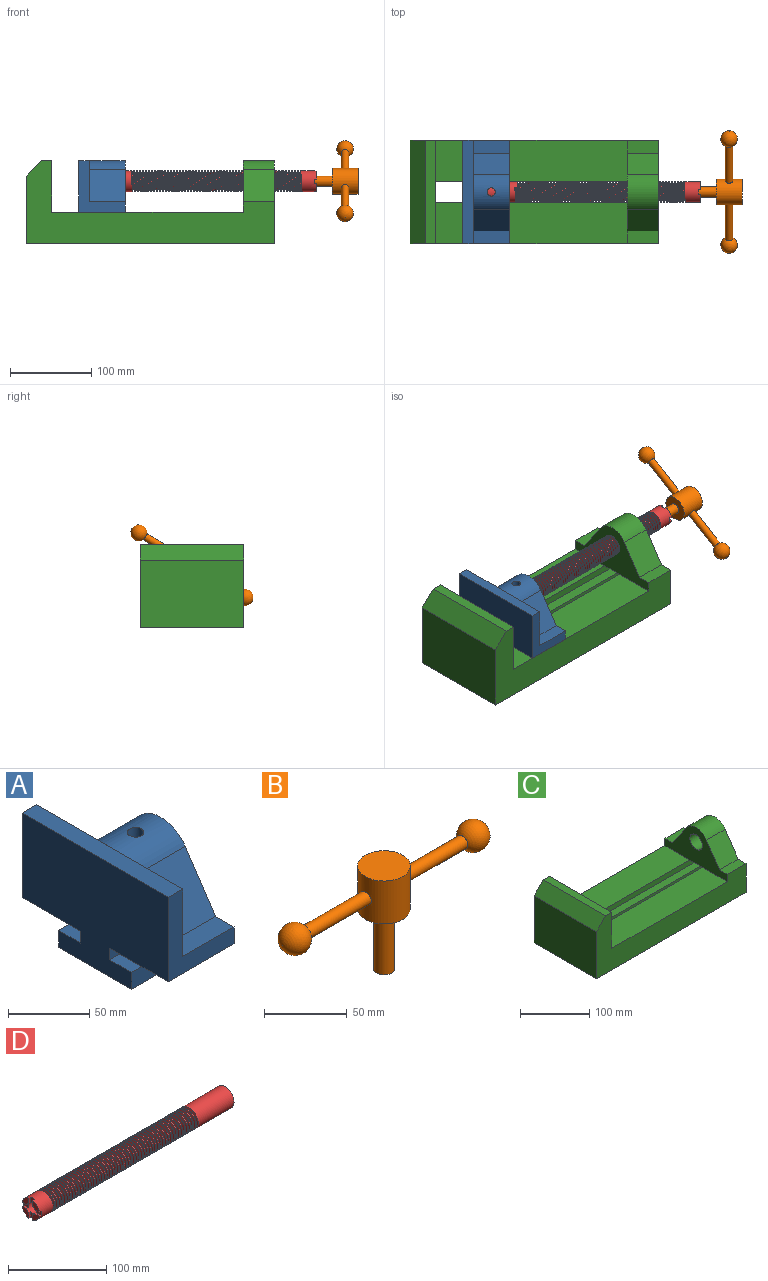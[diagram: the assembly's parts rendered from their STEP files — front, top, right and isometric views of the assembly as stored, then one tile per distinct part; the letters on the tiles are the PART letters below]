
ASSEMBLY  parts=4 mates=3
PART A: 24 faces, bbox 57.2x127x85.1 mm
  f0: cylinder r=25.4mm len=44.45mm, axis (1,0,0), area 2131.1mm2, adj f1,f7,f9,f11,f12,f23
  f1: plane 127x85.09mm, normal (1,0,0), area 5190mm2, adj f0,f2,f3,f5,f7,f8,f10,f11
  f2: plane 63.5x57.15mm, normal (0,0,-1), area 3629mm2, adj f1,f6,f18,f19
  f3: plane 63.5x57.15mm, normal (0,-1,0), area 1371mm2, adj f1,f4,f6,f10,f12,f22
  f4: plane 127x12.7mm, normal (0,0,1), area 1612.9mm2, adj f3,f5,f6,f9,f12
  f5: plane 63.5x57.15mm, normal (0,1,0), area 1371mm2, adj f1,f4,f6,f8,f9,f15
  f6: plane 127x85.09mm, normal (-1,0,0), area 9096.8mm2, adj f2,f3,f4,f5,f15,f16,f17,f18
  f7: plane 44.45x39.55mm, normal (0,0.83,0.56), area 2116.9mm2, adj f0,f1,f8,f9
  f8: plane 44.45x15.88mm, normal (0,0,1), area 705.6mm2, adj f1,f5,f7,f9
  f9: plane 63.5x50.8mm, normal (1,0,0), area 1700mm2, adj f0,f4,f5,f7,f8
  f10: plane 44.45x15.88mm, normal (0,0,1), area 705.6mm2, adj f1,f3,f11,f12
  f11: plane 44.45x39.55mm, normal (0,-0.83,0.56), area 2116.9mm2, adj f0,f1,f10,f12
  f12: plane 63.5x50.8mm, normal (1,0,0), area 1700mm2, adj f0,f3,f4,f10,f11
  f13: cylinder r=12.7mm len=44.45mm, axis (1,0,0), area 3464.1mm2, adj f1,f14,f23
  f14: plane 25.4x25.4mm, normal (1,0,0), area 506.7mm2, adj f13
  f15: plane 57.15x50.8mm, normal (0,0,-1), area 2903.2mm2, adj f1,f5,f6,f16
  f16: plane 57.15x8.89mm, normal (0,1,0), area 508.1mm2, adj f1,f6,f15,f17
  f17: plane 57.15x19.05mm, normal (0,0,1), area 1088.7mm2, adj f1,f6,f16,f18
  f18: plane 57.15x12.7mm, normal (0,1,0), area 725.8mm2, adj f1,f2,f6,f17
  f19: plane 57.15x12.7mm, normal (0,-1,0), area 725.8mm2, adj f1,f2,f6,f20
  f20: plane 57.15x19.05mm, normal (0,0,1), area 1088.7mm2, adj f1,f6,f19,f21
  f21: plane 57.15x8.89mm, normal (0,-1,0), area 508.1mm2, adj f1,f6,f20,f22
  f22: plane 57.15x50.8mm, normal (0,0,-1), area 2903.2mm2, adj f1,f3,f6,f21
  f23: cylinder r=5.08mm len=13.76mm, axis (0,0,1), area 413.9mm2, adj f0,f13
PART B: 9 faces, bbox 172.7x31.8x76.2 mm
  f0: cylinder r=4.45mm len=51.82mm, axis (-1,0,0), area 1438.5mm2, adj f2,f8
  f1: cylinder r=4.45mm len=51.82mm, axis (-1,0,0), area 1438.5mm2, adj f2,f7
  f2: cylinder r=15.88mm len=31.75mm, axis (0,0,1), area 3041.6mm2, adj f0,f1,f3,f4
  f3: plane 31.75x31.75mm, normal (0,0,-1), area 665.1mm2, adj f2,f5
  f4: plane 31.75x31.75mm, normal (0,0,1), area 791.7mm2, adj f2
  f5: cylinder r=6.35mm len=44.45mm, axis (0,0,1), area 1773.5mm2, adj f3,f6
  f6: plane 12.7x12.7mm, normal (0,0,-1), area 126.7mm2, adj f5
  f7: sphere r=10.16mm, area 1231.8mm2, adj f1
  f8: sphere r=10.16mm, area 1231.8mm2, adj f0
PART C: 28 faces, bbox 304.8x127x101.6 mm
  f0: plane 127x101.6mm, normal (1,0,0), area 7544.8mm2, adj f7,f8,f9,f10,f11,f12,f13,f14
  f1: plane 234.95x50.8mm, normal (0,0,1), area 11935.5mm2, adj f2,f4,f9,f21
  f2: plane 127x63.5mm, normal (-1,0,0), area 4157.7mm2, adj f1,f3,f8,f9,f10,f11,f12,f13
  f3: plane 234.95x50.8mm, normal (0,0,1), area 11935.5mm2, adj f2,f4,f8,f22
  f4: plane 127x101.6mm, normal (1,0,0), area 9516.1mm2, adj f1,f3,f5,f7,f8,f9,f17,f18
  f5: plane 127x12.7mm, normal (0,0,1), area 1612.9mm2, adj f4,f8,f9,f27
  f6: plane 127x82.55mm, normal (-1,0,0), area 10483.8mm2, adj f7,f8,f9,f27
  f7: plane 304.8x127mm, normal (0,0,-1), area 31774.1mm2, adj f0,f4,f6,f8,f9,f17,f26
  f8: plane 304.8x101.6mm, normal (0,-1,0), area 13931.4mm2, adj f0,f2,f3,f4,f5,f6,f7,f13
  f9: plane 304.8x101.6mm, normal (0,1,0), area 13931.4mm2, adj f0,f1,f2,f4,f5,f6,f7,f11
  f10: cylinder r=25.4mm len=42.19mm, axis (1,0,0), area 1896.6mm2, adj f0,f2,f12,f14
  f11: plane 38.1x15.88mm, normal (0,0,1), area 604.8mm2, adj f0,f2,f9,f12
  f12: plane 39.55x38.1mm, normal (0,0.83,0.56), area 1814.5mm2, adj f0,f2,f10,f11
  f13: plane 38.1x15.88mm, normal (0,0,1), area 604.8mm2, adj f0,f2,f8,f14
  f14: plane 39.55x38.1mm, normal (0,-0.83,0.56), area 1814.5mm2, adj f0,f2,f10,f13
  f15: cylinder r=12.7mm len=38.1mm, axis (1,0,0), area 3040.2mm2, adj f0,f2
  f16: plane 38.1x25.4mm, normal (0,0,-1), area 967.7mm2, adj f0,f2,f21,f22
  f17: plane 273.05x16.51mm, normal (0,-1,0), area 4508.1mm2, adj f0,f4,f7,f18
  f18: plane 273.05x19.05mm, normal (0,0,1), area 5201.6mm2, adj f0,f4,f17,f19
  f19: plane 273.05x12.7mm, normal (0,-1,0), area 3467.7mm2, adj f0,f4,f18,f20
  f20: plane 273.05x19.05mm, normal (0,0,-1), area 5201.6mm2, adj f0,f4,f19,f21
  f21: plane 273.05x8.89mm, normal (0,-1,0), area 2427.4mm2, adj f0,f1,f4,f16,f20
  f22: plane 273.05x8.89mm, normal (0,1,0), area 2427.4mm2, adj f0,f3,f4,f16,f23
  f23: plane 273.05x19.05mm, normal (0,0,-1), area 5201.6mm2, adj f0,f4,f22,f24
  f24: plane 273.05x12.7mm, normal (0,1,0), area 3467.7mm2, adj f0,f4,f23,f25
  f25: plane 273.05x19.05mm, normal (0,0,1), area 5201.6mm2, adj f0,f4,f24,f26
  f26: plane 273.05x16.51mm, normal (0,1,0), area 4508.1mm2, adj f0,f4,f7,f25
  f27: plane 127x19.05mm, normal (-0.71,0,0.71), area 3421.5mm2, adj f5,f6,f8,f9
PART D: 78 faces, bbox 279.4x25.4x29.3 mm
  f0: plane 9.9x9.9mm, normal (-1,0,0), area 62.3mm2, adj f4,f59,f68,f71
  f1: plane 9.9x9.9mm, normal (-1,0,0), area 62.3mm2, adj f4,f65,f69,f71
  f2: plane 9.9x9.9mm, normal (-1,0,0), area 62.3mm2, adj f4,f62,f66,f71
  f3: plane 9.9x9.9mm, normal (-1,0,0), area 62.3mm2, adj f4,f60,f63,f71
  f4: cylinder r=12.7mm len=25.4mm, axis (1,0,0), area 1598.5mm2, adj f0,f1,f2,f3,f5,f59,f60,f61
  f5: cylinder r=12.7mm len=25.4mm, axis (1,0,0), area 101.4mm2, adj f4,f6,f76,f77
  f6: cylinder r=12.7mm len=25.4mm, axis (1,0,0), area 101.4mm2, adj f5,f7,f76,f77
  f7: cylinder r=12.7mm len=25.4mm, axis (1,0,0), area 101.3mm2, adj f6,f8,f76,f77
  f8: cylinder r=12.7mm len=25.4mm, axis (1,0,0), area 101.3mm2, adj f7,f9,f76,f77
  f9: cylinder r=12.7mm len=25.4mm, axis (1,0,0), area 101.3mm2, adj f8,f10,f76,f77
  f10: cylinder r=12.7mm len=25.4mm, axis (1,0,0), area 101.3mm2, adj f9,f11,f76,f77
  f11: cylinder r=12.7mm len=25.4mm, axis (1,0,0), area 101.3mm2, adj f10,f12,f76,f77
  f12: cylinder r=12.7mm len=25.4mm, axis (1,0,0), area 101.4mm2, adj f11,f13,f76,f77
  f13: cylinder r=12.7mm len=25.4mm, axis (1,0,0), area 101.4mm2, adj f12,f14,f76,f77
  f14: cylinder r=12.7mm len=25.4mm, axis (1,0,0), area 101.3mm2, adj f13,f15,f76,f77
  f15: cylinder r=12.7mm len=25.4mm, axis (1,0,0), area 101.3mm2, adj f14,f16,f76,f77
  f16: cylinder r=12.7mm len=25.4mm, axis (1,0,0), area 101.3mm2, adj f15,f17,f76,f77
  f17: cylinder r=12.7mm len=25.4mm, axis (1,0,0), area 101.3mm2, adj f16,f18,f76,f77
  f18: cylinder r=12.7mm len=25.4mm, axis (1,0,0), area 101.3mm2, adj f17,f19,f76,f77
  f19: cylinder r=12.7mm len=25.4mm, axis (1,0,0), area 101.4mm2, adj f18,f20,f76,f77
  f20: cylinder r=12.7mm len=25.4mm, axis (1,0,0), area 101.4mm2, adj f19,f21,f76,f77
  f21: cylinder r=12.7mm len=25.4mm, axis (1,0,0), area 101.3mm2, adj f20,f22,f76,f77
  f22: cylinder r=12.7mm len=25.4mm, axis (1,0,0), area 101.3mm2, adj f21,f23,f76,f77
  f23: cylinder r=12.7mm len=25.4mm, axis (1,0,0), area 101.3mm2, adj f22,f24,f76,f77
  f24: cylinder r=12.7mm len=25.4mm, axis (1,0,0), area 101.3mm2, adj f23,f25,f76,f77
  f25: cylinder r=12.7mm len=25.4mm, axis (1,0,0), area 101.3mm2, adj f24,f26,f76,f77
  f26: cylinder r=12.7mm len=25.4mm, axis (1,0,0), area 101.4mm2, adj f25,f27,f76,f77
  f27: cylinder r=12.7mm len=25.4mm, axis (1,0,0), area 101.4mm2, adj f26,f28,f76,f77
  f28: cylinder r=12.7mm len=25.4mm, axis (1,0,0), area 101.3mm2, adj f27,f29,f76,f77
  f29: cylinder r=12.7mm len=25.4mm, axis (1,0,0), area 101.3mm2, adj f28,f30,f76,f77
  f30: cylinder r=12.7mm len=25.4mm, axis (1,0,0), area 101.3mm2, adj f29,f31,f76,f77
  f31: cylinder r=12.7mm len=25.4mm, axis (1,0,0), area 101.3mm2, adj f30,f32,f76,f77
  f32: cylinder r=12.7mm len=25.4mm, axis (1,0,0), area 101.3mm2, adj f31,f33,f76,f77
  f33: cylinder r=12.7mm len=25.4mm, axis (1,0,0), area 101.4mm2, adj f32,f34,f76,f77
  f34: cylinder r=12.7mm len=25.4mm, axis (1,0,0), area 101.4mm2, adj f33,f35,f76,f77
  f35: cylinder r=12.7mm len=25.4mm, axis (1,0,0), area 101.3mm2, adj f34,f36,f76,f77
  f36: cylinder r=12.7mm len=25.4mm, axis (1,0,0), area 101.3mm2, adj f35,f37,f76,f77
  f37: cylinder r=12.7mm len=25.4mm, axis (1,0,0), area 101.3mm2, adj f36,f38,f76,f77
  f38: cylinder r=12.7mm len=25.4mm, axis (1,0,0), area 101.3mm2, adj f37,f39,f76,f77
  f39: cylinder r=12.7mm len=25.4mm, axis (1,0,0), area 101.3mm2, adj f38,f40,f76,f77
  f40: cylinder r=12.7mm len=25.4mm, axis (1,0,0), area 101.4mm2, adj f39,f41,f76,f77
  f41: cylinder r=12.7mm len=25.4mm, axis (1,0,0), area 101.4mm2, adj f40,f42,f76,f77
  f42: cylinder r=12.7mm len=25.4mm, axis (1,0,0), area 101.3mm2, adj f41,f43,f76,f77
  f43: cylinder r=12.7mm len=25.4mm, axis (1,0,0), area 101.3mm2, adj f42,f44,f76,f77
  f44: cylinder r=12.7mm len=25.4mm, axis (1,0,0), area 101.3mm2, adj f43,f45,f76,f77
  f45: cylinder r=12.7mm len=25.4mm, axis (1,0,0), area 101.3mm2, adj f44,f46,f76,f77
  f46: cylinder r=12.7mm len=25.4mm, axis (1,0,0), area 101.3mm2, adj f45,f47,f76,f77
  f47: cylinder r=12.7mm len=25.4mm, axis (1,0,0), area 101.4mm2, adj f46,f48,f76,f77
  f48: cylinder r=12.7mm len=25.4mm, axis (1,0,0), area 101.4mm2, adj f47,f49,f76,f77
  f49: cylinder r=12.7mm len=25.4mm, axis (1,0,0), area 101.3mm2, adj f48,f50,f76,f77
  f50: cylinder r=12.7mm len=25.4mm, axis (1,0,0), area 101.3mm2, adj f49,f51,f76,f77
  f51: cylinder r=12.7mm len=25.4mm, axis (1,0,0), area 101.3mm2, adj f50,f52,f76,f77
  f52: cylinder r=12.7mm len=25.4mm, axis (1,0,0), area 101.3mm2, adj f51,f53,f76,f77
  f53: cylinder r=12.7mm len=25.4mm, axis (1,0,0), area 101.3mm2, adj f52,f54,f76,f77
  f54: cylinder r=12.7mm len=25.4mm, axis (1,0,0), area 101.4mm2, adj f53,f55,f76,f77
  f55: cylinder r=12.7mm len=25.4mm, axis (1,0,0), area 101.4mm2, adj f54,f56,f76,f77
  f56: cylinder r=12.7mm len=25.4mm, axis (1,0,0), area 101.3mm2, adj f55,f57,f76,f77
  f57: cylinder r=12.7mm len=57.98mm, axis (1,0,0), area 4315.2mm2, adj f56,f58,f74,f76,f77
  f58: plane 25.4x25.4mm, normal (1,0,0), area 506.7mm2, adj f57
  f59: plane 6.62x2.54mm, normal (0,0,-1), area 16.8mm2, adj f0,f4,f61,f71
  f60: plane 6.62x2.54mm, normal (0,0,1), area 16.8mm2, adj f3,f4,f61,f71
  f61: plane 6.88x5.08mm, normal (-1,0,0), area 32.7mm2, adj f4,f59,f60,f71
  f62: plane 6.62x2.54mm, normal (0,-1,0), area 16.8mm2, adj f2,f4,f64,f71
  f63: plane 6.62x2.54mm, normal (0,1,0), area 16.8mm2, adj f3,f4,f64,f71
  f64: plane 6.88x5.08mm, normal (-1,0,0), area 32.7mm2, adj f4,f62,f63,f71
  f65: plane 6.62x2.54mm, normal (0,0,-1), area 16.8mm2, adj f1,f4,f67,f71
  f66: plane 6.62x2.54mm, normal (0,0,1), area 16.8mm2, adj f2,f4,f67,f71
  f67: plane 6.88x5.08mm, normal (-1,0,0), area 32.7mm2, adj f4,f65,f66,f71
  f68: plane 6.62x2.54mm, normal (0,1,0), area 16.8mm2, adj f0,f4,f70,f71
  f69: plane 6.62x2.54mm, normal (0,-1,0), area 16.8mm2, adj f1,f4,f70,f71
  f70: plane 6.88x5.08mm, normal (-1,0,0), area 32.7mm2, adj f4,f68,f69,f71
  f71: cylinder r=6.35mm len=25.4mm, axis (-1,0,0), area 960.3mm2, adj f0,f1,f2,f3,f59,f60,f61,f62
  f72: plane 12.7x12.7mm, normal (-1,0,0), area 126.7mm2, adj f71
  f73: plane 2.54x2.54mm, normal (0,0,1), area 4.8mm2, adj f4,f75,f76,f77
  f74: plane 2.55x2.33mm, normal (0,-0.41,0.91), area 4.8mm2, adj f57,f75,f76,f77
  f75: cylinder r=10.16mm len=209.17mm, axis (1,0,0), area 4414.6mm2, adj f73,f74,f76,f77
  f76: bspline ~208.92x29.33mm, area 10273.8mm2, adj f4,f5,f6,f7,f8,f9,f10,f11
  f77: bspline ~208.92x29.33mm, area 10275.9mm2, adj f4,f5,f6,f7,f8,f9,f10,f11
PLACE A rot(axis=(-1,0,0),0deg) t=(-265.32,0,16.51)mm
PLACE B rot(axis=(0.66,0.37,0.66),139.4deg) t=(1.38,0,76.2)mm
PLACE C at identity fixed
PLACE D rot(axis=(0,0.71,-0.71),180deg) t=(-252.62,59.69,76.2)mm
MATE slider C.f4 <-> A.f6  axis (1,0,0) through (-120.65,-63.5,38.1)mm
MATE revolute B.f2 <-> D.f4  axis (-1,0,0) through (179.18,0,76.2)mm
MATE fastened A.f0 <-> D.f4  axis (1,0,0) through (-74.82,0,76.2)mm
